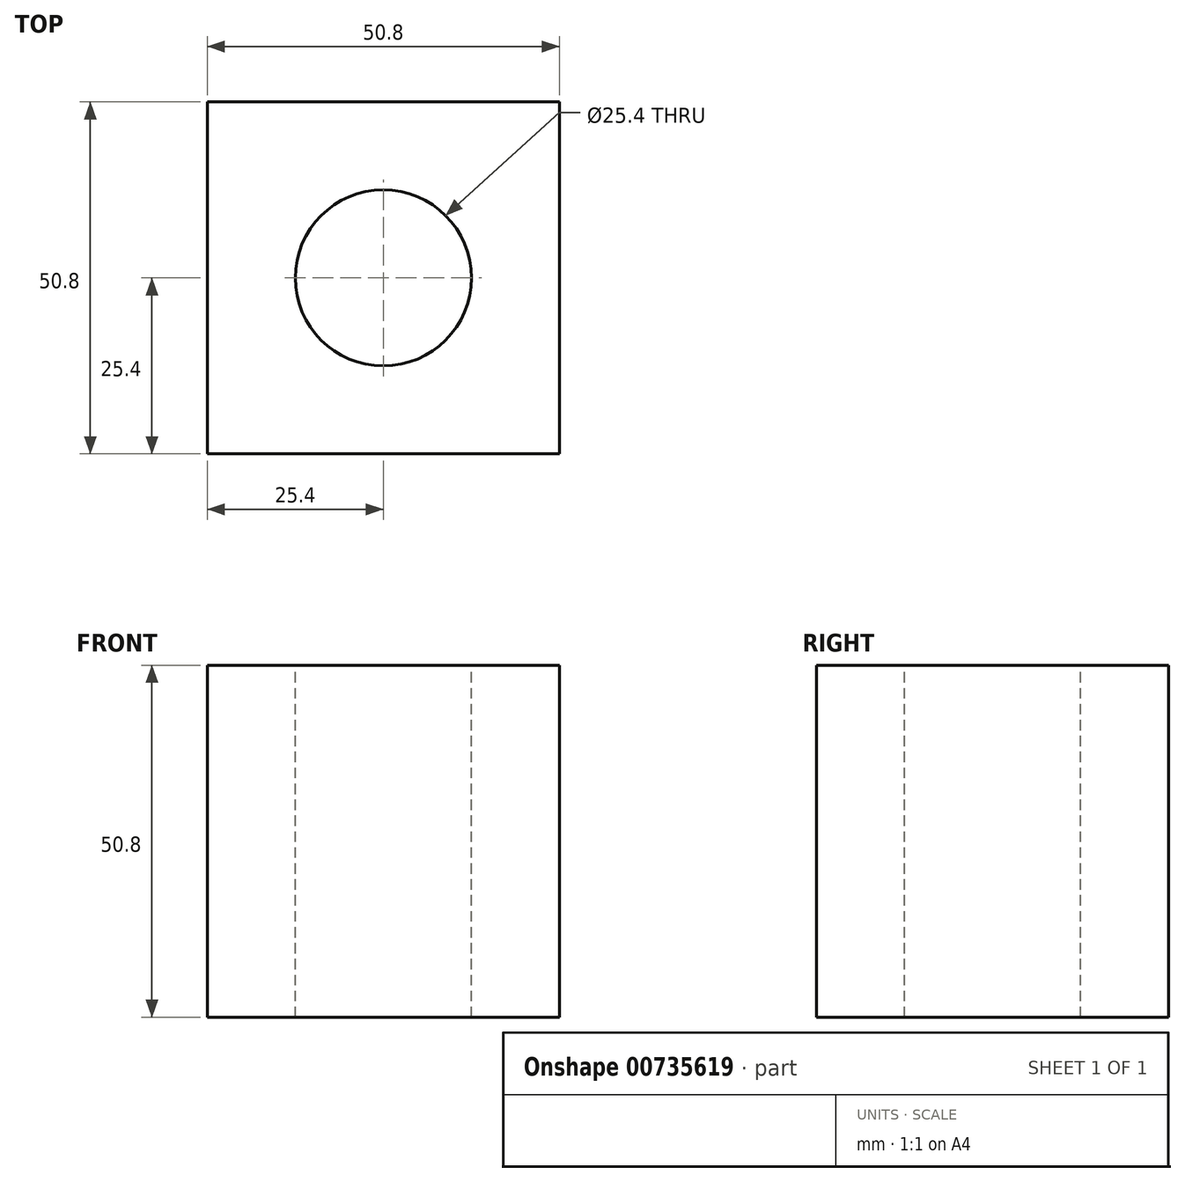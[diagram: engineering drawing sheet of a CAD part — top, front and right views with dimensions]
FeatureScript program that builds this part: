
annotation { "Feature Type Name" : "Feature", "Feature Type Description" : "" }
export const myFeature = defineFeature(function(context is Context, id is Id, definition is map)
    precondition{}
    {
        {
            var Q0;
            Q0=qCreatedBy(makeId("Front.planeOp"),FACE);
            var sketch = newSketch(context, id + "F0", { "sketchPlane" : qUnion([Q0])});
            skLineSegment(sketch, "E0", {"start": v(0, 0) * mm, "end": v(50.8, 0) * mm});
            skLineSegment(sketch, "E1", {"start": v(50.8, 0) * mm, "end": v(50.8, 50.8) * mm});
            skLineSegment(sketch, "E2", {"start": v(50.8, 50.8) * mm, "end": v(0, 50.8) * mm});
            skLineSegment(sketch, "E3", {"start": v(0, 50.8) * mm, "end": v(0, 0) * mm});
            skSolve(sketch);
        }
        {
            var Q0;
            Q0=makeQuery(id+"F0.imprint","IMPRINT",FACE,{"disambiguationData":[TD([[makeQuery(id+"F0.imprint","IMPRINT",EDGE,{"derivedFrom":sQuery(id+"F0.wireOp",EDGE,"E0")}),1.0]])]});
            extrude(context, id + "F1", {"entities" : qUnion([Q0]), "depth" : 50.8 * mm, "offsetDistance" : 25.4 * mm});
        }
        {
            var Q0;
            Q0=makeQuery(id+"F1.opExtrude","SWEPT_FACE",FACE,{"disambiguationData":[OSD([sQuery(id+"F0.wireOp",EDGE,"E2")])]});
            var sketch = newSketch(context, id + "F2", { "sketchPlane" : qUnion([Q0])});
            skLineSegment(sketch, "E4", {"start": v(23.08, -25.3) * mm, "end": v(10.38, -47.3) * mm});
            skLineSegment(sketch, "E5", {"start": v(10.38, -47.3) * mm, "end": v(35.78, -47.3) * mm});
            skLineSegment(sketch, "E6", {"start": v(35.78, -47.3) * mm, "end": v(23.08, -25.3) * mm});
            skSolve(sketch);
        }
        {
            var Q0;
            Q0 = qSketchRegion(id + "F2", true);
            extrude(context, id + "F3", {"entities" : qUnion([Q0]), "operationType" : NewBodyOperationType.ADD, "oppositeDirection" : true, "depth" : 25.4 * mm, "offsetDistance" : 25.4 * mm});
        }
        {
            var Q0;
            Q0=makeQuery(id+"F1.opExtrude","SWEPT_FACE",FACE,{"disambiguationData":[OSD([sQuery(id+"F0.wireOp",EDGE,"E2")])]});
            var sketch = newSketch(context, id + "F4", { "sketchPlane" : qUnion([Q0])});
            skSolve(sketch);
        }
        {
            var Q0;
            {var subQ0=sQuery(id+"F0.wireOp",EDGE,"E2");Q0=makeQuery(id+"F4.imprint","IMPRINT",FACE,{"disambiguationData":[TD([[makeQuery(id+"F4.imprint","IMPRINT",EDGE,{"derivedFrom":makeQuery(id+"F1.opExtrude","CAP_EDGE",EDGE,{"disambiguationData":[OSD([subQ0])],"isStart":true})}),1.0]])]});}
            var sketch = newSketch(context, id + "F5", { "sketchPlane" : qUnion([Q0])});
            skCircle(sketch, "E7", {"center": v(25.4, -25.4) * mm, "radius": 12.7 * mm});
            skSolve(sketch);
        }
        {
            var Q0;
            Q0 = qSketchRegion(id + "F5", true);
            extrude(context, id + "F6", {"entities" : qUnion([Q0]), "operationType" : NewBodyOperationType.REMOVE, "oppositeDirection" : true, "depth" : 50.8 * mm, "offsetDistance" : 25.4 * mm});
        }
    });
